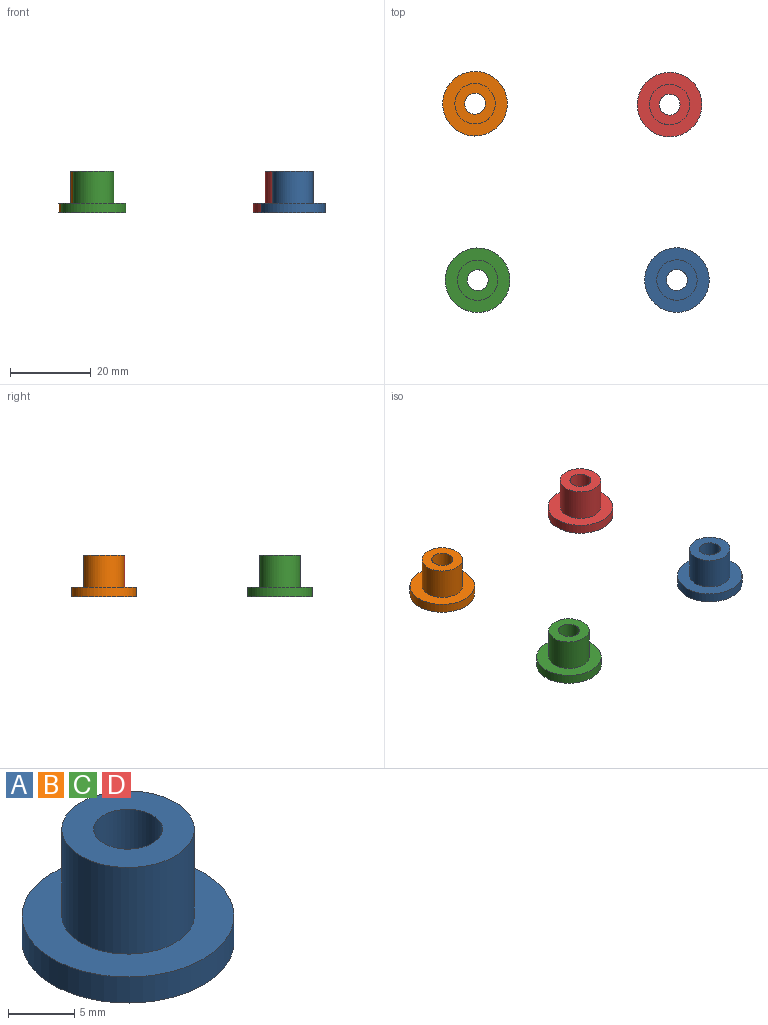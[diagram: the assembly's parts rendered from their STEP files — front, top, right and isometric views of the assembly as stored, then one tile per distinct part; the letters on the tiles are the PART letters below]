
ASSEMBLY  parts=4 mates=3
PART A: 6 faces, bbox 16x16x10.4 mm
  f0: cylinder r=2.6mm len=10.4mm, axis (0,0,-1), area 169.9mm2, adj f2,f4
  f1: cylinder r=5mm len=10mm, axis (0,0,-1), area 251.3mm2, adj f2,f5
  f2: plane 10x10mm, normal (0,0,1), area 57.3mm2, adj f0,f1
  f3: cylinder r=8mm len=16mm, axis (0,0,1), area 120.6mm2, adj f4,f5
  f4: plane 16x16mm, normal (0,0,-1), area 179.8mm2, adj f0,f3
  f5: plane 16x16mm, normal (0,0,1), area 122.5mm2, adj f1,f3
PART B: same geometry as A
PART C: same geometry as A
PART D: same geometry as A
PLACE A t=(24.62,-22.13,-3.46)mm
PLACE B t=(-25.42,21.57,-3.46)mm
PLACE C t=(-24.77,-22.17,-3.46)mm
PLACE D t=(22.79,21.35,-3.46)mm
MATE planar A.f3 <-> B.f3  axis (0,0,-1) through (24.62,-22.13,-5.86)mm
MATE planar D.f3 <-> B.f3  axis (0,0,-1) through (22.79,21.35,-5.86)mm
MATE planar C.f3 <-> B.f3  axis (0,0,-1) through (-24.77,-22.17,-5.86)mm
